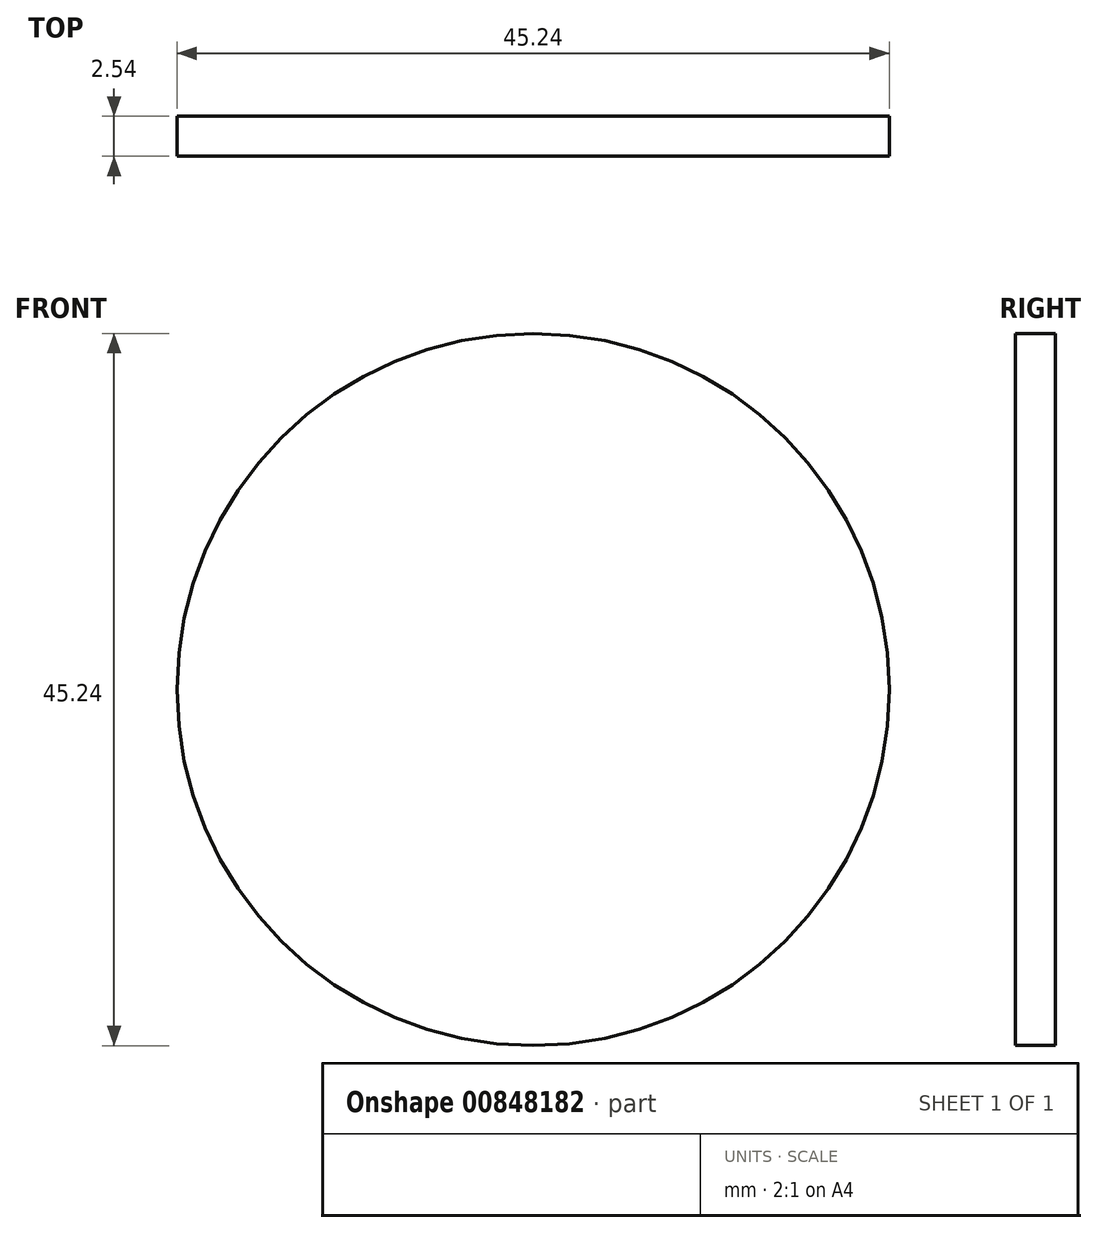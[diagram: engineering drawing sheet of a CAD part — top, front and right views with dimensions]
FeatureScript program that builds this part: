
annotation { "Feature Type Name" : "Feature", "Feature Type Description" : "" }
export const myFeature = defineFeature(function(context is Context, id is Id, definition is map)
    precondition{}
    {
        {
            var Q0;
            Q0=qCreatedBy(makeId("Front.planeOp"),FACE);
            var sketch = newSketch(context, id + "F0", { "sketchPlane" : qUnion([Q0])});
            skCircle(sketch, "E0", {"center": v(0, 0) * mm, "radius": 22.62 * mm});
            skSolve(sketch);
        }
        {
            var Q0;
            Q0=makeQuery(id+"F0.imprint","IMPRINT",FACE,{"disambiguationData":[TD([[makeQuery(id+"F0.imprint","IMPRINT",EDGE,{"derivedFrom":sQuery(id+"F0.wireOp",EDGE,"E0")}),1.0]])]});
            var Q1;
            Q1=sQuery(id+"F0.wireOp",EDGE,"E0");
            extrude(context, id + "F1", {"entities" : qUnion([Q0]), "surfaceEntities" : qUnion([Q1]), "depth" : 2.54 * mm, "offsetDistance" : 25.4 * mm});
        }
    });
